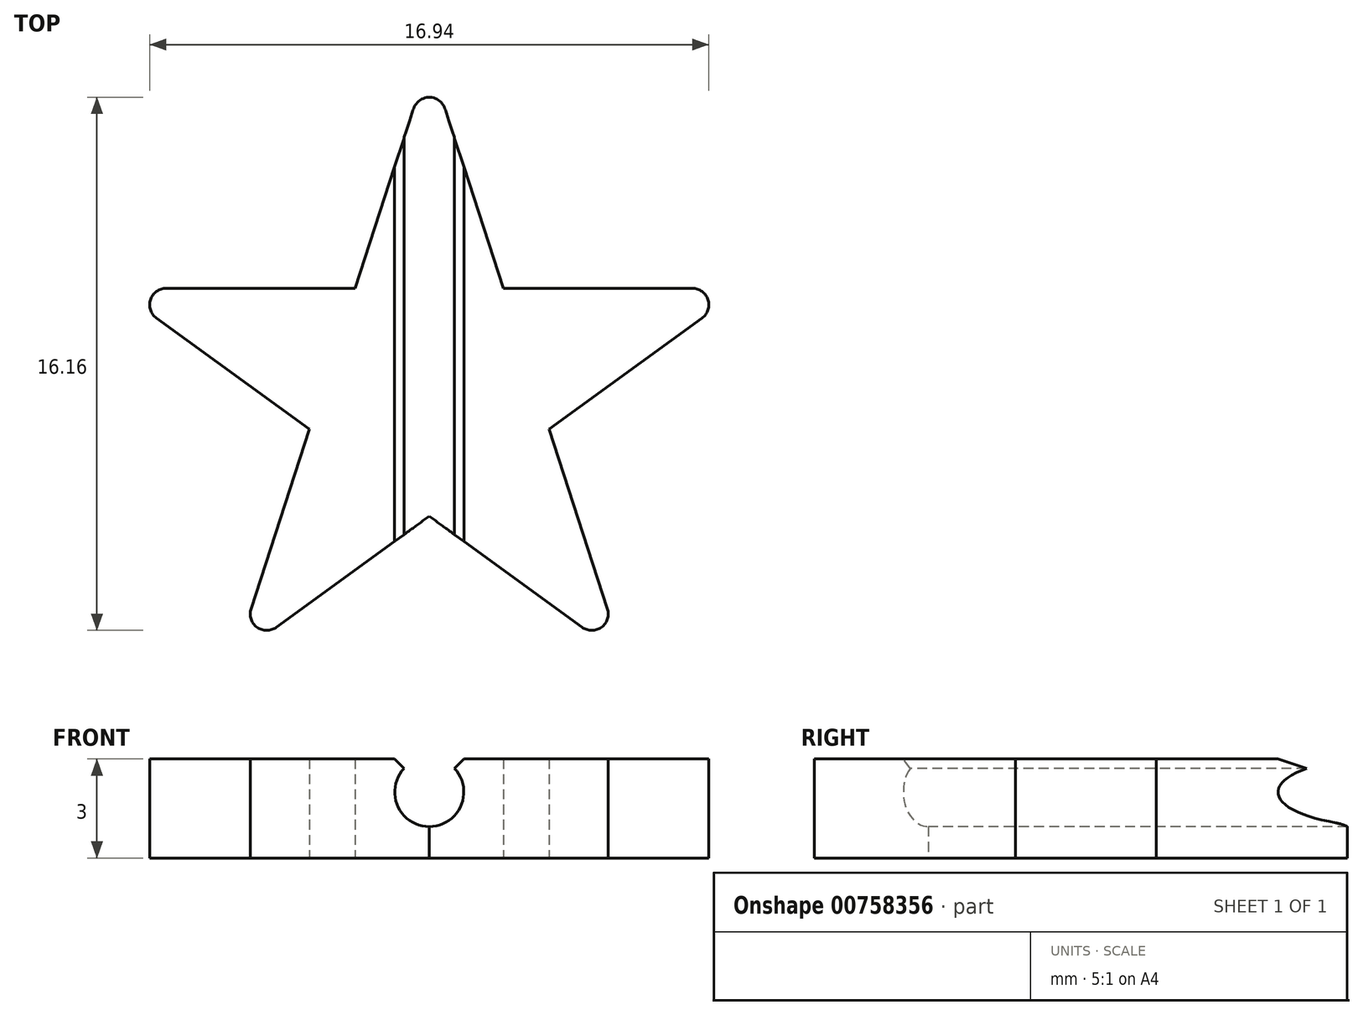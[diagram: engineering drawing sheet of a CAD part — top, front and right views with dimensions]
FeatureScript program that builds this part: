
annotation { "Feature Type Name" : "Feature", "Feature Type Description" : "" }
export const myFeature = defineFeature(function(context is Context, id is Id, definition is map)
    precondition{}
    {
        {
            var Q0;
            Q0=qCreatedBy(makeId("Top.planeOp"),FACE);
            var sketch = newSketch(context, id + "F0", { "sketchPlane" : qUnion([Q0])});
            skCircle(sketch, "E0.cCircle", {"center": v(0, 0) * mm, "radius": 10 * mm, "construction": true});
            skLineSegment(sketch, "E0.0", {"start": v(0, 10) * mm, "end": v(9.51, 3.1) * mm, "construction": true});
            skLineSegment(sketch, "E0.1", {"start": v(9.51, 3.1) * mm, "end": v(5.88, -8.1) * mm, "construction": true});
            skLineSegment(sketch, "E0.2", {"start": v(5.88, -8.1) * mm, "end": v(-5.88, -8.1) * mm, "construction": true});
            skLineSegment(sketch, "E0.3", {"start": v(-5.88, -8.1) * mm, "end": v(-9.51, 3.1) * mm, "construction": true});
            skLineSegment(sketch, "E0.4", {"start": v(-9.51, 3.1) * mm, "end": v(0, 10) * mm, "construction": true});
            skLineSegment(sketch, "E1", {"start": v(9.51, 3.1) * mm, "end": v(-9.51, 3.1) * mm});
            skLineSegment(sketch, "E2", {"start": v(9.51, 3.1) * mm, "end": v(-5.88, -8.1) * mm});
            skLineSegment(sketch, "E3", {"start": v(5.88, -8.1) * mm, "end": v(0, 10) * mm});
            skLineSegment(sketch, "E4", {"start": v(0, 10) * mm, "end": v(-5.88, -8.1) * mm});
            skLineSegment(sketch, "E5", {"start": v(5.88, -8.1) * mm, "end": v(-9.51, 3.1) * mm});
            skSolve(sketch);
        }
        {
            var Q0;
            Q0 = qSketchRegion(id + "F0", true);
            extrude(context, id + "F1", {"entities" : qUnion([Q0]), "depth" : 3 * mm, "offsetDistance" : 25 * mm});
        }
        {
            var Q0;
            Q0=makeQuery(id+"F1.opExtrude","CAP_FACE",FACE,{"disambiguationData":[OSD([sQuery(id+"F0.wireOp",EDGE,"E1"),sQuery(id+"F0.wireOp",EDGE,"E2"),sQuery(id+"F0.wireOp",EDGE,"E3"),sQuery(id+"F0.wireOp",EDGE,"E4"),sQuery(id+"F0.wireOp",EDGE,"E5")])],"isStart":false});
            var sketch = newSketch(context, id + "F2", { "sketchPlane" : qUnion([Q0])});
            skLineSegment(sketch, "E6.bottom", {"start": v(-2, 3.1) * mm, "end": v(2, 3.1) * mm});
            skLineSegment(sketch, "E6.top", {"start": v(-2, -3.1) * mm, "end": v(2, -3.1) * mm});
            skLineSegment(sketch, "E6.left", {"start": v(-2, 3.1) * mm, "end": v(-2, -3.1) * mm});
            skLineSegment(sketch, "E6.right", {"start": v(2, 3.1) * mm, "end": v(2, -3.1) * mm});
            skPoint(sketch, "E6.middle", {"position": v(0, 0) * mm});
            skSolve(sketch);
        }
        {
            var Q0;
            Q0 = qSketchRegion(id + "F2", true);
            var Q1;
            Q1=makeQuery(id+"F2.imprint","IMPRINT",FACE,{"disambiguationData":[TD([[makeQuery(id+"F2.imprint","IMPRINT",EDGE,{"derivedFrom":sQuery(id+"F2.wireOp",EDGE,"E6.bottom")}),1.0]])]});
            extrude(context, id + "F3", {"entities" : qUnion([Q0, Q1]), "operationType" : NewBodyOperationType.ADD, "depth" : 1 * mm, "offsetDistance" : 25 * mm});
        }
        {
            var Q0;
            Q0=qCreatedBy(makeId("Front.planeOp"),FACE);
            var sketch = newSketch(context, id + "F4", { "sketchPlane" : qUnion([Q0])});
            skLineSegment(sketch, "E7.0", {"start": v(-1.5, 3) * mm, "end": v(1.5, 3) * mm, "construction": true});
            skLineSegment(sketch, "E8", {"start": v(0, 3) * mm, "end": v(0, 3) * mm});
            skCircle(sketch, "E9", {"center": v(0, 3) * mm, "radius": 1.05 * mm});
            skLineSegment(sketch, "E10", {"start": v(-0.75, 5) * mm, "end": v(-0.75, 3.73) * mm});
            skLineSegment(sketch, "E11.MirrorCS", {"start": v(0.75, 5) * mm, "end": v(0.75, 3.73) * mm});
            skLineSegment(sketch, "E12", {"start": v(-0.75, 5) * mm, "end": v(0.75, 5) * mm});
            skLineSegment(sketch, "E13", {"start": v(0, 0) * mm, "end": v(0, 4.48) * mm, "construction": true});
            skSolve(sketch);
        }
        {
            var Q0;
            Q0 = qSketchRegion(id + "F4", true);
            var Q1;
            Q1=makeQuery(id+"F3.opExtrude","SWEPT_FACE",FACE,{"disambiguationData":[OSD([sQuery(id+"F2.wireOp",EDGE,"E6.bottom")])]});
            extrude(context, id + "F5", {"entities" : qUnion([Q0]), "operationType" : NewBodyOperationType.REMOVE, "endBound" : BoundingType.THROUGH_ALL, "oppositeDirection" : true, "depth" : 25 * mm, "endBoundEntityFace" : qUnion([Q1]), "offsetDistance" : 25 * mm, "hasSecondDirection" : true, "secondDirectionBound" : SecondDirectionBoundingType.THROUGH_ALL, "secondDirectionOppositeDirection" : false, "secondDirectionDepth" : 25 * mm});
        }
        {
            var Q0;
            Q0=makeQuery(id+"F1.opExtrude","SWEPT_EDGE",EDGE,{"disambiguationData":[OSD([sQuery(id+"F0.wireOp",EDGE,"E3"),sQuery(id+"F0.wireOp",EDGE,"E5")])]});
            var Q1;
            Q1=makeQuery(id+"F1.opExtrude","SWEPT_EDGE",EDGE,{"disambiguationData":[OSD([sQuery(id+"F0.wireOp",EDGE,"E1"),sQuery(id+"F0.wireOp",EDGE,"E2")])]});
            var Q2;
            Q2=makeQuery(id+"F1.opExtrude","SWEPT_EDGE",EDGE,{"disambiguationData":[OSD([sQuery(id+"F0.wireOp",EDGE,"E3"),sQuery(id+"F0.wireOp",EDGE,"E4")])]});
            var Q3;
            Q3=makeQuery(id+"F1.opExtrude","SWEPT_EDGE",EDGE,{"disambiguationData":[OSD([sQuery(id+"F0.wireOp",EDGE,"E1"),sQuery(id+"F0.wireOp",EDGE,"E5")])]});
            var Q4;
            Q4=makeQuery(id+"F1.opExtrude","SWEPT_EDGE",EDGE,{"disambiguationData":[OSD([sQuery(id+"F0.wireOp",EDGE,"E2"),sQuery(id+"F0.wireOp",EDGE,"E4")])]});
            fillet(context, id + "F6", {"entities" : qUnion([Q0, Q1, Q2, Q3, Q4]), "radius" : 0.5 * mm, "tangentPropagation" : true, "allowEdgeOverflow" : false});
        }
        {
            var Q0;
            Q0=makeQuery(id+"F5.boolean.opBoolean","INTERSECT",EDGE,{"derivedFrom":[makeQuery(id+"F3.opExtrude","CAP_FACE",FACE,{"disambiguationData":[OSD([sQuery(id+"F0.wireOp",EDGE,"E1"),sQuery(id+"F0.wireOp",EDGE,"E2"),sQuery(id+"F0.wireOp",EDGE,"E3"),sQuery(id+"F0.wireOp",EDGE,"E4"),sQuery(id+"F0.wireOp",EDGE,"E5")])],"isStart":false}),makeQuery(id+"F5.opExtrude","SWEPT_FACE",FACE,{"disambiguationData":[OSD([sQuery(id+"F4.wireOp",EDGE,"E10")])]})]});
            var Q1;
            Q1=makeQuery(id+"F5.boolean.opBoolean","INTERSECT",EDGE,{"derivedFrom":[makeQuery(id+"F3.opExtrude","CAP_FACE",FACE,{"disambiguationData":[OSD([sQuery(id+"F0.wireOp",EDGE,"E1"),sQuery(id+"F0.wireOp",EDGE,"E2"),sQuery(id+"F0.wireOp",EDGE,"E3"),sQuery(id+"F0.wireOp",EDGE,"E4"),sQuery(id+"F0.wireOp",EDGE,"E5")])],"isStart":false}),makeQuery(id+"F5.opExtrude","SWEPT_FACE",FACE,{"disambiguationData":[OSD([sQuery(id+"F4.wireOp",EDGE,"E11.MirrorCS")])]})]});
            chamfer(context, id + "F7", {"entities" : qUnion([Q0, Q1]), "width" : 0.3 * mm, "tangentPropagation" : true});
        }
        {
            var Q0;
            Q0=makeQuery(id+"F1.opExtrude","CAP_FACE",FACE,{"disambiguationData":[OSD([sQuery(id+"F0.wireOp",EDGE,"E1"),sQuery(id+"F0.wireOp",EDGE,"E2"),sQuery(id+"F0.wireOp",EDGE,"E3"),sQuery(id+"F0.wireOp",EDGE,"E4"),sQuery(id+"F0.wireOp",EDGE,"E5")])],"isStart":true});
            extrude(context, id + "F8", {"entities" : qUnion([Q0]), "operationType" : NewBodyOperationType.REMOVE, "oppositeDirection" : true, "depth" : 1 * mm, "offsetDistance" : 25 * mm});
        }
    });
